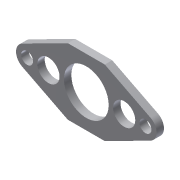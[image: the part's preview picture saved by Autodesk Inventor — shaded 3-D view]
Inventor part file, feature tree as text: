
AUTODESK INVENTOR PART (.ipt)
format: ipt  version: 2013 (Build 170138000, 138)  size: 104,448 bytes
history: native  units: in
note: dims shown in document units (in); Inventor stores cm internally (conversion verified against a paired STEP export)
features: extrude x1, sketch x1
ambient origin geometry x8: Origin, YZ Plane, XZ Plane, XY Plane, X Axis, Y Axis, Z Axis, Center Point
bodies: Solid1 (feature_tree)
feature tree (2):
  extrude  "Extrusion1"  Depth=0.375in
  sketch  "Sketch1"  dims[d0=0.756in d1=0.375in d2=0.64in d3=0.64in d4=0.625in d5=0.201in d6=1.0in d7=0.188in d8=1.12in d9=0.201in d10=1.0in d11=0.188in d12=0.56in d13=0.125in d14=0.0in]
